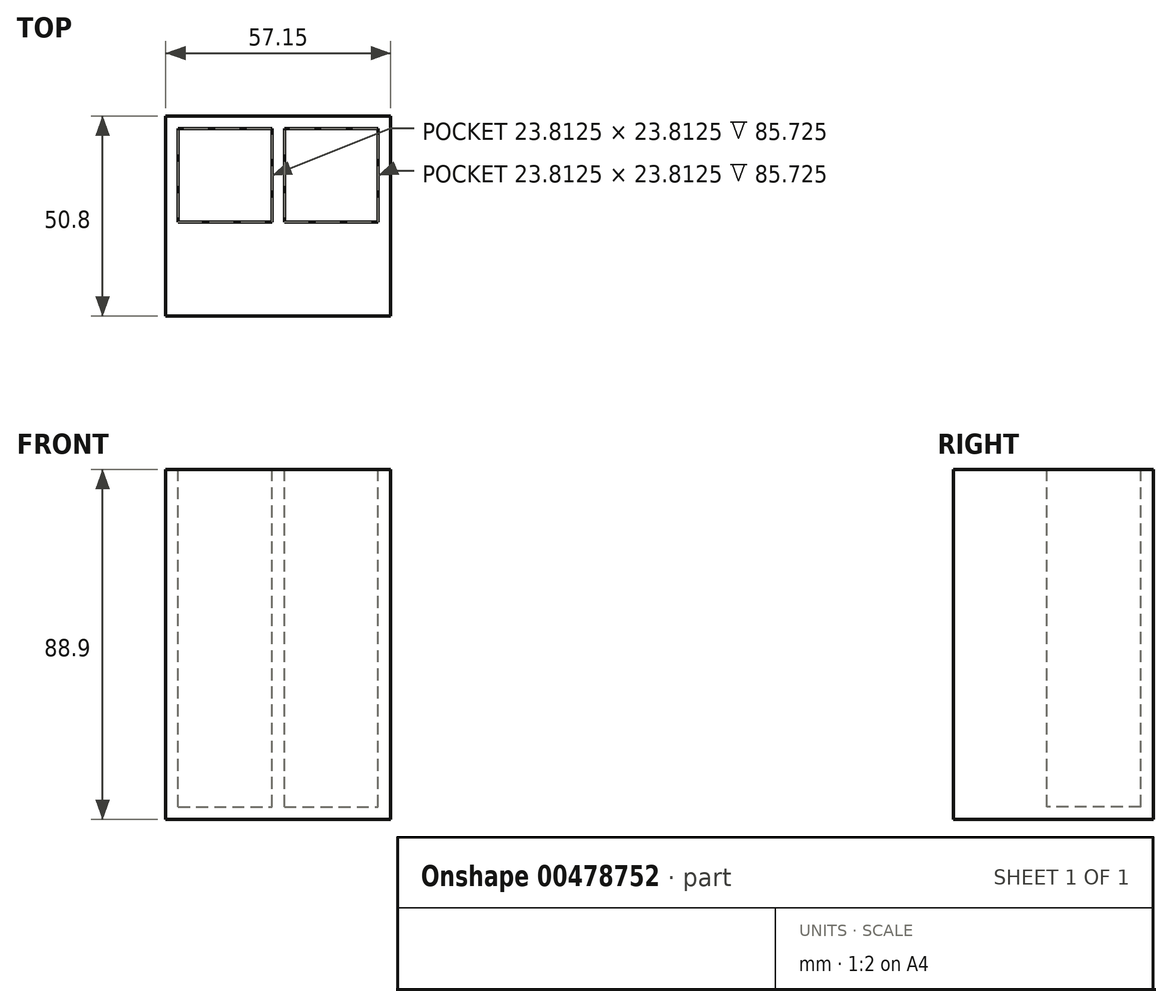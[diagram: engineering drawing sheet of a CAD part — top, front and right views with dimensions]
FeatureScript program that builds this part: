
annotation { "Feature Type Name" : "Feature", "Feature Type Description" : "" }
export const myFeature = defineFeature(function(context is Context, id is Id, definition is map)
    precondition{}
    {
        {
            var Q0;
            Q0=qCreatedBy(makeId("Front.planeOp"),FACE);
            var sketch = newSketch(context, id + "F0", { "sketchPlane" : qUnion([Q0])});
            skLineSegment(sketch, "E0.bottom", {"start": v(-39.87, 72.06) * mm, "end": v(17.28, 72.06) * mm});
            skLineSegment(sketch, "E0.top", {"start": v(-39.87, -16.84) * mm, "end": v(17.28, -16.84) * mm});
            skLineSegment(sketch, "E0.left", {"start": v(-39.87, 72.06) * mm, "end": v(-39.87, -16.84) * mm});
            skLineSegment(sketch, "E0.right", {"start": v(17.28, 72.06) * mm, "end": v(17.28, -16.84) * mm});
            skSolve(sketch);
        }
        {
            var Q0;
            Q0=makeQuery(id+"F0.imprint","IMPRINT",FACE,{"disambiguationData":[TD([[makeQuery(id+"F0.imprint","IMPRINT",EDGE,{"derivedFrom":sQuery(id+"F0.wireOp",EDGE,"E0.bottom")}),-1.0]])]});
            extrude(context, id + "F1", {"entities" : qUnion([Q0]), "depth" : 50.8 * mm});
        }
        {
            var Q0;
            Q0=makeQuery(id+"F1.opExtrude","SWEPT_FACE",FACE,{"disambiguationData":[OSD([sQuery(id+"F0.wireOp",EDGE,"E0.bottom")])]});
            var sketch = newSketch(context, id + "F2", { "sketchPlane" : qUnion([Q0])});
            skLineSegment(sketch, "E1.bottom", {"start": v(-36.7, -3.18) * mm, "end": v(-12.89, -3.18) * mm});
            skLineSegment(sketch, "E1.top", {"start": v(-36.7, -26.99) * mm, "end": v(-12.89, -26.99) * mm});
            skLineSegment(sketch, "E1.left", {"start": v(-36.7, -3.18) * mm, "end": v(-36.7, -26.99) * mm});
            skLineSegment(sketch, "E1.right", {"start": v(-12.89, -3.17) * mm, "end": v(-12.89, -26.99) * mm});
            skSolve(sketch);
        }
        {
            var Q0;
            Q0=makeQuery(id+"F2.imprint","IMPRINT",FACE,{"disambiguationData":[TD([[makeQuery(id+"F2.imprint","IMPRINT",EDGE,{"derivedFrom":sQuery(id+"F2.wireOp",EDGE,"E1.bottom")}),-1.0]])]});
            extrude(context, id + "F3", {"entities" : qUnion([Q0]), "operationType" : NewBodyOperationType.REMOVE, "oppositeDirection" : true, "depth" : 85.72 * mm});
        }
        {
            var Q0;
            Q0=makeQuery(id+"F1.opExtrude","SWEPT_FACE",FACE,{"disambiguationData":[OSD([sQuery(id+"F0.wireOp",EDGE,"E0.bottom")])]});
            var sketch = newSketch(context, id + "F4", { "sketchPlane" : qUnion([Q0])});
            skSolve(sketch);
        }
        {
            var Q0;
            {var subQ0=sQuery(id+"F0.wireOp",EDGE,"E0.bottom");Q0=makeQuery(id+"F4.imprint","IMPRINT",FACE,{"disambiguationData":[TD([[makeQuery(id+"F4.imprint","IMPRINT",EDGE,{"derivedFrom":makeQuery(id+"F1.opExtrude","CAP_EDGE",EDGE,{"disambiguationData":[OSD([subQ0])],"isStart":true})}),-1.0]])]});}
            var sketch = newSketch(context, id + "F5", { "sketchPlane" : qUnion([Q0])});
            skLineSegment(sketch, "E2.bottom", {"start": v(-9.71, -3.18) * mm, "end": v(14.1, -3.18) * mm});
            skLineSegment(sketch, "E2.top", {"start": v(-9.71, -26.99) * mm, "end": v(14.1, -26.99) * mm});
            skLineSegment(sketch, "E2.left", {"start": v(-9.71, -3.18) * mm, "end": v(-9.71, -26.99) * mm});
            skLineSegment(sketch, "E2.right", {"start": v(14.1, -3.17) * mm, "end": v(14.1, -26.99) * mm});
            skSolve(sketch);
        }
        {
            var Q0;
            Q0=makeQuery(id+"F5.imprint","IMPRINT",FACE,{"disambiguationData":[TD([[makeQuery(id+"F5.imprint","IMPRINT",EDGE,{"derivedFrom":sQuery(id+"F5.wireOp",EDGE,"E2.bottom")}),-1.0]])]});
            extrude(context, id + "F6", {"entities" : qUnion([Q0]), "operationType" : NewBodyOperationType.REMOVE, "oppositeDirection" : true, "depth" : 85.72 * mm});
        }
    });
